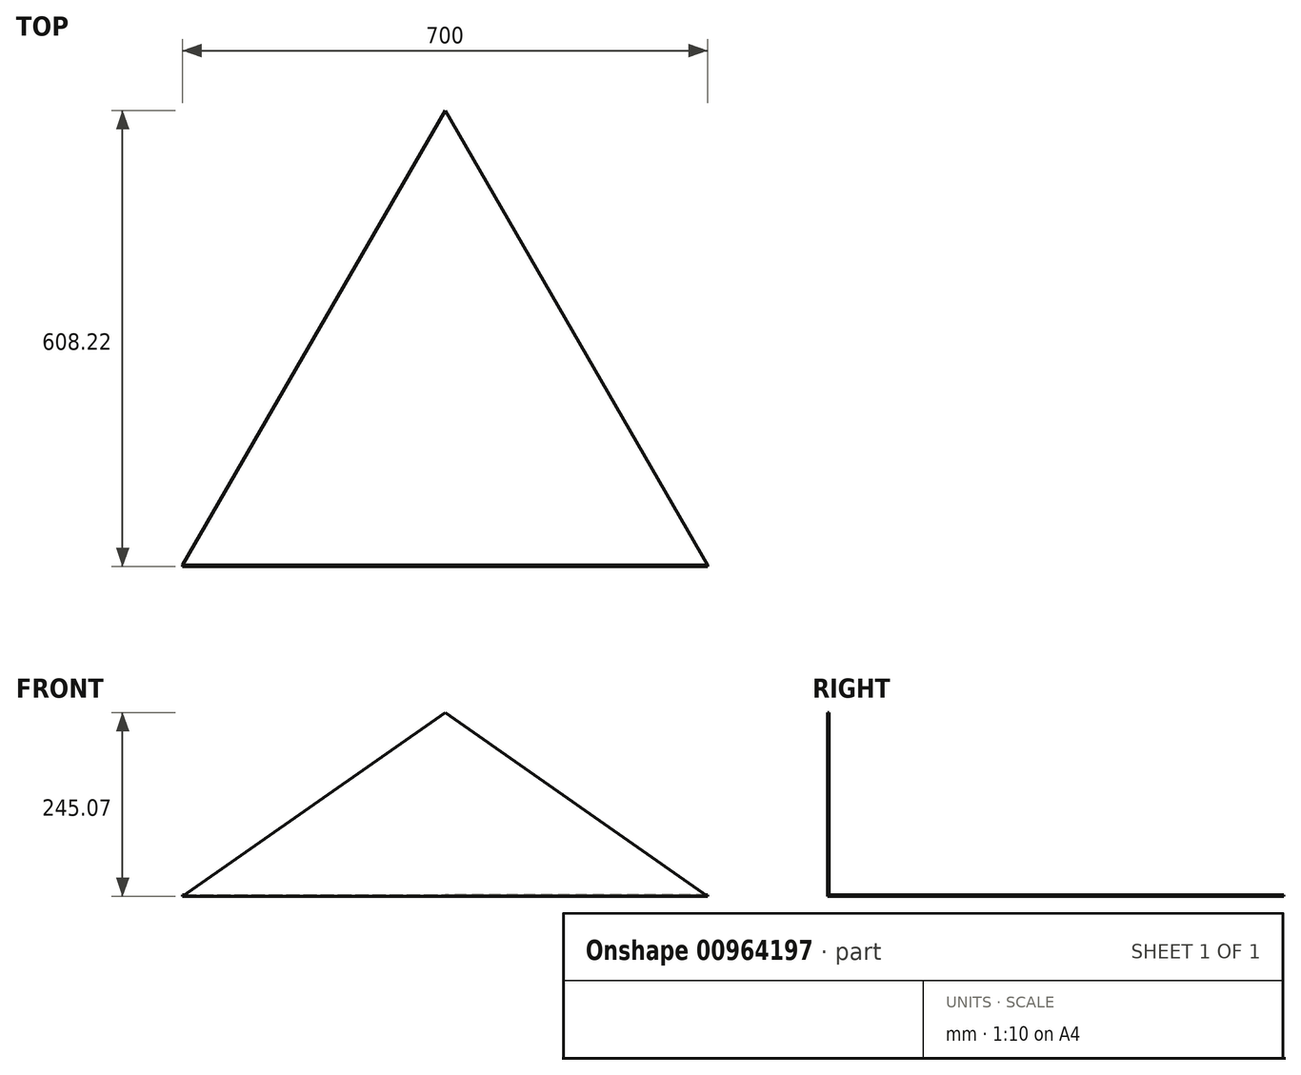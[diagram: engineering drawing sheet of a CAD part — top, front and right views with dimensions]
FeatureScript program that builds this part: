
annotation { "Feature Type Name" : "Feature", "Feature Type Description" : "" }
export const myFeature = defineFeature(function(context is Context, id is Id, definition is map)
    precondition{}
    {
        {
            var Q0;
            Q0=qCreatedBy(makeId("Front.planeOp"),FACE);
            var sketch = newSketch(context, id + "F0", { "sketchPlane" : qUnion([Q0])});
            skLineSegment(sketch, "E0", {"start": v(0, 0) * mm, "end": v(350, 0) * mm});
            skLineSegment(sketch, "E1", {"start": v(350, 0) * mm, "end": v(0, 245.07) * mm});
            skLineSegment(sketch, "E2", {"start": v(0, 245.07) * mm, "end": v(-350, 0) * mm});
            skLineSegment(sketch, "E3", {"start": v(-350, 0) * mm, "end": v(0, 0) * mm});
            skSolve(sketch);
        }
        {
            var Q0;
            Q0=makeQuery(id+"F0.imprint","IMPRINT",FACE,{"disambiguationData":[TD([[makeQuery(id+"F0.imprint","IMPRINT",EDGE,{"derivedFrom":sQuery(id+"F0.wireOp",EDGE,"E0")}),1.0]])]});
            extrude(context, id + "F1", {"entities" : qUnion([Q0]), "depth" : 2 * mm, "offsetDistance" : 25 * mm});
        }
        {
            var Q0;
            Q0=qCreatedBy(makeId("Top.planeOp"),FACE);
            var sketch = newSketch(context, id + "F2", { "sketchPlane" : qUnion([Q0])});
            skLineSegment(sketch, "E4", {"start": v(350, 0) * mm, "end": v(0, 606.22) * mm});
            skLineSegment(sketch, "E5", {"start": v(-350, 0) * mm, "end": v(0, 606.22) * mm});
            skLineSegment(sketch, "E6", {"start": v(-350, 0) * mm, "end": v(350, 0) * mm});
            skSolve(sketch);
        }
        {
            var Q0;
            Q0=makeQuery(id+"F2.imprint","IMPRINT",FACE,{"disambiguationData":[TD([[makeQuery(id+"F2.imprint","IMPRINT",EDGE,{"derivedFrom":sQuery(id+"F2.wireOp",EDGE,"E4")}),1.0]])]});
            extrude(context, id + "F3", {"entities" : qUnion([Q0]), "operationType" : NewBodyOperationType.ADD, "depth" : 2 * mm, "offsetDistance" : 25 * mm});
        }
    });
